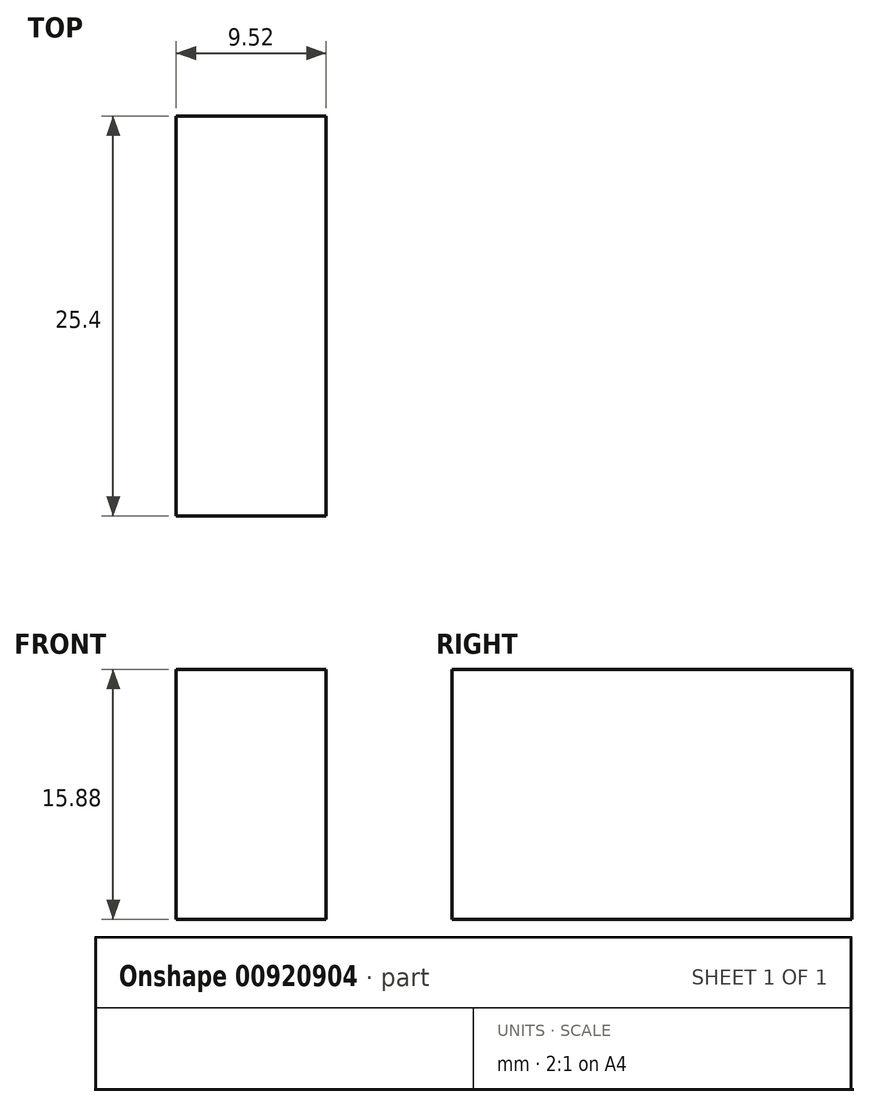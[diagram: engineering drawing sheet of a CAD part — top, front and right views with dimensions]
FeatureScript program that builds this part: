
annotation { "Feature Type Name" : "Feature", "Feature Type Description" : "" }
export const myFeature = defineFeature(function(context is Context, id is Id, definition is map)
    precondition{}
    {
        {
            var Q0;
            Q0=qCreatedBy(makeId("Top.planeOp"),FACE);
            var sketch = newSketch(context, id + "F0", { "sketchPlane" : qUnion([Q0])});
            skLineSegment(sketch, "E0.bottom", {"start": v(-7.05, 35.82) * mm, "end": v(2.47, 35.82) * mm});
            skLineSegment(sketch, "E0.top", {"start": v(-7.05, 10.42) * mm, "end": v(2.47, 10.42) * mm});
            skLineSegment(sketch, "E0.left", {"start": v(-7.05, 35.82) * mm, "end": v(-7.05, 10.42) * mm});
            skLineSegment(sketch, "E0.right", {"start": v(2.47, 35.82) * mm, "end": v(2.47, 10.42) * mm});
            skSolve(sketch);
        }
        {
            var Q0;
            Q0=makeQuery(id+"F0.imprint","IMPRINT",FACE,{"disambiguationData":[TD([[makeQuery(id+"F0.imprint","IMPRINT",EDGE,{"derivedFrom":sQuery(id+"F0.wireOp",EDGE,"E0.bottom")}),-1.0]])]});
            extrude(context, id + "F1", {"entities" : qUnion([Q0]), "depth" : 15.88 * mm, "offsetDistance" : 25.4 * mm});
        }
    });
